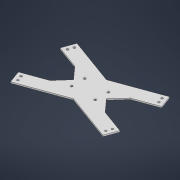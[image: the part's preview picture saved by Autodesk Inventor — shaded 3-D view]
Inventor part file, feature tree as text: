
AUTODESK INVENTOR PART (.ipt)
format: ipt  version: 2021 (Build 250183000, 183)  size: 145,408 bytes
history: native  units: mm
features: extrude x3, sketch x3
ambient origin geometry x8: Origin, YZ Plane, XZ Plane, XY Plane, X Axis, Y Axis, Z Axis, Center Point
bodies: Volumenkörper1 (feature_tree)
feature tree (6):
  extrude  "Extrusion1"  Depth=50.0mm
  extrude  "Extrusion2"  Depth=3.490659mm
  extrude  "Extrusion3"  TaperAngle=90.0deg  [1 undecoded]
  sketch  "Skizze1"  dims[d0=50.0mm d1=50.0mm]
  sketch  "Skizze2"  dims[d3=75.0mm d6=3.490659mm]
  sketch  "Skizze3"  dims[d7=20.0mm d8=90.0deg d12=7.306589mm d13=2.0mm d14=0.0mm d15=3.2mm d16=6.0mm d17=6.0mm d18=3.2mm d19=6.0mm d20=6.0mm d21=2.0mm d22=0.0mm d23=3.2mm d24=18.0mm d25=10.0mm d26=2.0mm d27=0.0mm]
note: 1 required parameter value undecoded (feature->parameter linkage not recoverable at this tier; creation-order binding heuristic only, values carry confidence <= 0.55)
